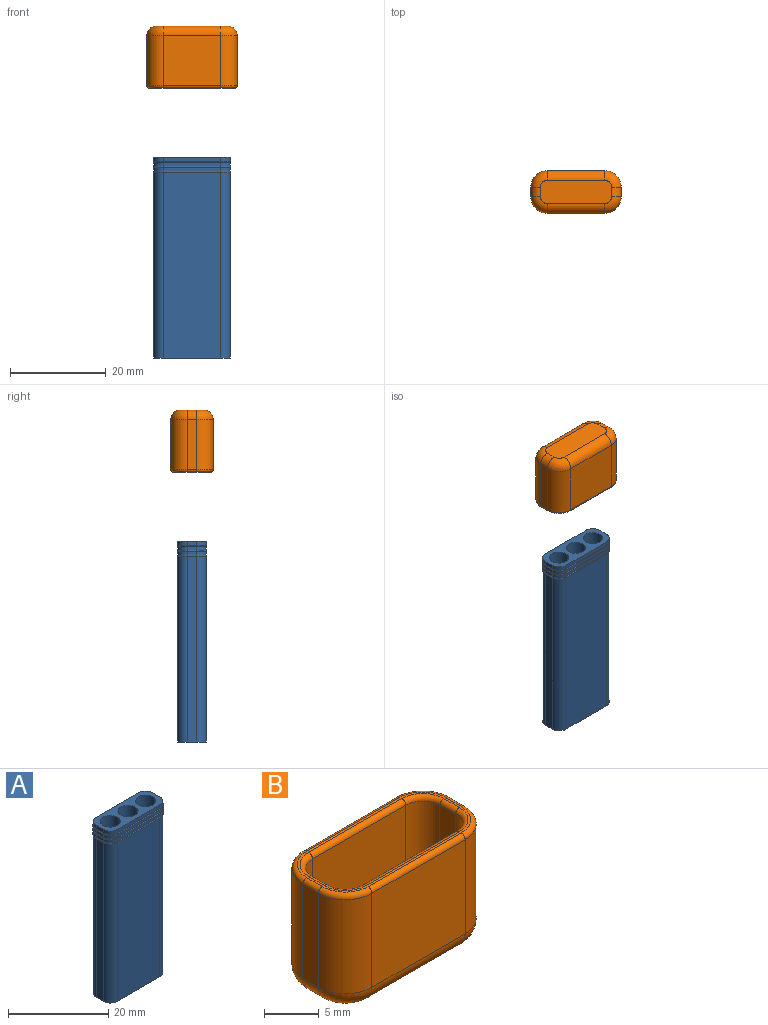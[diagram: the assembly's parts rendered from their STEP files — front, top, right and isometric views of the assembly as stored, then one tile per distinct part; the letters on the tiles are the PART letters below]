
ASSEMBLY  parts=2 mates=1
PART A: 124 faces, bbox 16.6x6.6x42 mm
  f0: plane 12x0.75mm, normal (0,-1,0), area 9mm2, adj f2,f5,f10,f47
  f1: plane 2x0.75mm, normal (-1,0,0), area 1.5mm2, adj f4,f5,f11,f48
  f2: cylinder r=2mm len=2mm, axis (0,0,-1), area 2.4mm2, adj f0,f9,f14,f51
  f3: cylinder r=2mm len=2mm, axis (0,0,1), area 2.4mm2, adj f8,f9,f12,f49
  f4: cylinder r=2mm len=2mm, axis (0,0,-1), area 2.4mm2, adj f1,f8,f16,f53
  f5: cylinder r=2mm len=2mm, axis (0,0,1), area 2.4mm2, adj f0,f1,f15,f52
  f6: plane 2x0.75mm, normal (1,0,0), area 1.5mm2, adj f13,f18,f19,f27
  f7: plane 12x0.75mm, normal (0,1,0), area 9mm2, adj f17,f19,f21,f31
  f8: plane 12x0.75mm, normal (0,1,0), area 9mm2, adj f3,f4,f17,f54
  f9: plane 2x0.75mm, normal (1,0,0), area 1.5mm2, adj f2,f3,f13,f50
  f10: cylinder r=0.12mm len=12mm, axis (1,0,0), area 4.7mm2, adj f0,f14,f15,f23
  f11: cylinder r=0.12mm len=2mm, axis (0,-1,0), area 0.8mm2, adj f1,f15,f16,f22
  f12: torus R=2mm, axis (0,0,1), area 1.3mm2, adj f3,f13,f17,f19
  f13: cylinder r=0.12mm len=2mm, axis (0,1,0), area 0.8mm2, adj f6,f9,f12,f14
  f14: torus R=2mm, axis (0,0,1), area 1.3mm2, adj f2,f10,f13,f18
  f15: torus R=2mm, axis (0,0,1), area 1.3mm2, adj f5,f10,f11,f20
  f16: torus R=2mm, axis (0,0,1), area 1.3mm2, adj f4,f11,f17,f21
  f17: cylinder r=0.12mm len=12mm, axis (-1,0,0), area 4.7mm2, adj f7,f8,f12,f16
  f18: cylinder r=2mm len=2mm, axis (0,0,-1), area 2.4mm2, adj f6,f14,f23,f28
  f19: cylinder r=2mm len=2mm, axis (0,0,1), area 2.4mm2, adj f6,f7,f12,f26
  f20: cylinder r=2mm len=2mm, axis (0,0,1), area 2.4mm2, adj f15,f22,f23,f29
  f21: cylinder r=2mm len=2mm, axis (0,0,-1), area 2.4mm2, adj f7,f16,f22,f30
  f22: plane 2x0.75mm, normal (-1,0,0), area 1.5mm2, adj f11,f20,f21,f24
  f23: plane 12x0.75mm, normal (0,-1,0), area 9mm2, adj f10,f18,f20,f25
  f24: cylinder r=0.12mm len=2mm, axis (0,-1,0), area 0.8mm2, adj f22,f29,f30,f41
  f25: cylinder r=0.12mm len=12mm, axis (1,0,0), area 4.7mm2, adj f23,f28,f29,f43
  f26: torus R=2mm, axis (0,0,1), area 1.3mm2, adj f19,f27,f31,f45
  f27: cylinder r=0.12mm len=2mm, axis (0,1,0), area 0.8mm2, adj f6,f26,f28,f39
  f28: torus R=2mm, axis (0,0,1), area 1.3mm2, adj f18,f25,f27,f46
  f29: torus R=2mm, axis (0,0,1), area 1.3mm2, adj f20,f24,f25,f44
  f30: torus R=2mm, axis (0,0,1), area 1.3mm2, adj f21,f24,f31,f42
  f31: cylinder r=0.12mm len=12mm, axis (-1,0,0), area 4.7mm2, adj f7,f26,f30,f40
  f32: plane 2x2mm, normal (0,0,1), area 3.1mm2, adj f123
  f33: plane 2x2mm, normal (0,0,1), area 3.1mm2, adj f122
  f34: plane 2x2mm, normal (0,0,1), area 3.1mm2, adj f121
  f35: cylinder r=2mm len=39mm, axis (0,0,-1), area 490.1mm2, adj f38,f123
  f36: cylinder r=2mm len=39mm, axis (0,0,-1), area 490.1mm2, adj f38,f122
  f37: cylinder r=2mm len=39mm, axis (0,0,-1), area 490.1mm2, adj f38,f121
  f38: plane 16x6mm, normal (0,0,1), area 54.9mm2, adj f35,f36,f37,f39,f40,f41,f42,f43
  f39: plane 2x0.88mm, normal (1,0,0), area 1.8mm2, adj f27,f38,f45,f46
  f40: plane 12x0.88mm, normal (0,1,0), area 10.5mm2, adj f31,f38,f42,f45
  f41: plane 2x0.88mm, normal (-1,0,0), area 1.8mm2, adj f24,f38,f42,f44
  f42: cylinder r=2mm len=2mm, axis (0,0,-1), area 2.7mm2, adj f30,f38,f40,f41
  f43: plane 12x0.88mm, normal (0,-1,0), area 10.5mm2, adj f25,f38,f44,f46
  f44: cylinder r=2mm len=2mm, axis (0,0,1), area 2.7mm2, adj f29,f38,f41,f43
  f45: cylinder r=2mm len=2mm, axis (0,0,1), area 2.7mm2, adj f26,f38,f39,f40
  f46: cylinder r=2mm len=2mm, axis (0,0,-1), area 2.7mm2, adj f28,f38,f39,f43
  f47: cylinder r=0.12mm len=12mm, axis (1,0,0), area 4.7mm2, adj f0,f51,f52,f118
  f48: cylinder r=0.12mm len=2mm, axis (0,-1,0), area 0.8mm2, adj f1,f52,f53,f116
  f49: torus R=2mm, axis (0,0,1), area 1.3mm2, adj f3,f50,f54,f113
  f50: cylinder r=0.12mm len=2mm, axis (0,1,0), area 0.8mm2, adj f9,f49,f51,f119
  f51: torus R=2mm, axis (0,0,1), area 1.3mm2, adj f2,f47,f50,f117
  f52: torus R=2mm, axis (0,0,1), area 1.3mm2, adj f5,f47,f48,f115
  f53: torus R=2mm, axis (0,0,1), area 1.3mm2, adj f4,f48,f54,f114
  f54: cylinder r=0.12mm len=12mm, axis (-1,0,0), area 4.7mm2, adj f8,f49,f53,f120
  f55: plane 4.39x3.01mm, normal (0,1,0), area 6.3mm2, adj f56,f57,f58,f59,f60,f61
  f56: extruded ~1.75x0.25mm, area 0.4mm2, adj f55,f57,f61,f65
  f57: plane 0.25x0.04mm, normal (1,0,0), area 0mm2, adj f55,f56,f58,f65
  f58: extruded ~0.86x0.49mm, area 0.2mm2, adj f55,f57,f59,f65
  f59: plane 3.53x2.48mm, normal (0.58,0,-0.82), area 1.1mm2, adj f55,f58,f60,f65
  f60: plane 2.96x0.25mm, normal (-1,0,0), area 0.7mm2, adj f55,f59,f61,f65
  f61: plane 2.64x0.25mm, normal (0,0,1), area 0.7mm2, adj f55,f56,f60,f65
  f62: plane 7.93x7.86mm, normal (0,1,0), area 26.9mm2, adj f66,f67,f68,f69,f70,f71,f72,f73
  f63: plane 7.93x2.86mm, normal (0,1,0), area 8.6mm2, adj f84,f85,f86,f87,f88,f89,f90,f91
  f64: plane 1.47x1.31mm, normal (0,1,0), area 1.6mm2, adj f93,f94,f95,f96,f97,f98,f99,f100
  f65: plane 7.98x5.9mm, normal (0,1,0), area 15.2mm2, adj f56,f57,f58,f59,f60,f61,f101,f102
  f66: plane 7.02x2.71mm, normal (0.36,0,-0.93), area 1.9mm2, adj f62,f67,f83,f120
  f67: plane 0.25x0.04mm, normal (1,0,0), area 0mm2, adj f62,f66,f68,f120
  f68: extruded ~1.91x0.25mm, area 0.5mm2, adj f62,f67,f69,f120
  f69: plane 5.11x0.25mm, normal (0,0,1), area 1.3mm2, adj f62,f68,f70,f120
  f70: plane 0.92x0.25mm, normal (1,0,0), area 0.2mm2, adj f62,f69,f71,f120
  f71: plane 7.93x0.25mm, normal (0,0,-1), area 2mm2, adj f62,f70,f72,f120
  f72: plane 1.38x0.25mm, normal (-1,0,0), area 0.3mm2, adj f62,f71,f73,f120
  f73: plane 6.54x2.53mm, normal (-0.36,0,0.93), area 1.8mm2, adj f62,f72,f74,f120
  f74: plane 0.25x0.04mm, normal (-1,0,0), area 0mm2, adj f62,f73,f75,f120
  f75: plane 6.54x2.51mm, normal (-0.36,0,-0.93), area 1.8mm2, adj f62,f74,f76,f120
  f76: plane 1.39x0.25mm, normal (-1,0,0), area 0.3mm2, adj f62,f75,f77,f120
  f77: plane 7.93x0.25mm, normal (0,0,1), area 2mm2, adj f62,f76,f78,f120
  f78: plane 0.85x0.25mm, normal (1,0,0), area 0.2mm2, adj f62,f77,f79,f120
  f79: plane 5.05x0.25mm, normal (0,0,-1), area 1.3mm2, adj f62,f78,f80,f120
  f80: extruded ~1.99x0.25mm, area 0.5mm2, adj f62,f79,f81,f120
  f81: plane 0.25x0.04mm, normal (1,0,0), area 0mm2, adj f62,f80,f82,f120
  f82: plane 7.03x2.69mm, normal (0.36,0,0.93), area 1.9mm2, adj f62,f81,f83,f120
  f83: plane 0.74x0.25mm, normal (1,0,0), area 0.2mm2, adj f62,f66,f82,f120
  f84: plane 0.76x0.25mm, normal (-1,0,0), area 0.2mm2, adj f63,f85,f92,f120
  f85: plane 2.1x1.62mm, normal (-0.79,0,0.61), area 0.7mm2, adj f63,f84,f86,f120
  f86: plane 0.62x0.48mm, normal (0.61,0,0.79), area 0.2mm2, adj f63,f85,f87,f120
  f87: extruded ~1.29x1.06mm, area 0.4mm2, adj f63,f86,f88,f120
  f88: extruded ~0.25x0.25mm, area 0.1mm2, adj f63,f87,f89,f120
  f89: extruded ~1.34x0.25mm, area 0.3mm2, adj f63,f88,f90,f120
  f90: plane 5.65x0.25mm, normal (0,0,1), area 1.4mm2, adj f63,f89,f91,f120
  f91: plane 0.88x0.25mm, normal (1,0,0), area 0.2mm2, adj f63,f90,f92,f120
  f92: plane 7.93x0.25mm, normal (0,0,-1), area 2mm2, adj f63,f84,f91,f120
  f93: extruded ~0.46x0.25mm, area 0.1mm2, adj f64,f94,f100,f120
  f94: extruded ~0.49x0.25mm, area 0.1mm2, adj f64,f93,f95,f120
  f95: extruded ~0.54x0.25mm, area 0.1mm2, adj f64,f94,f96,f120
  f96: extruded ~0.55x0.25mm, area 0.1mm2, adj f64,f95,f97,f120
  f97: extruded ~0.49x0.25mm, area 0.1mm2, adj f64,f96,f98,f120
  f98: extruded ~0.48x0.25mm, area 0.1mm2, adj f64,f97,f99,f120
  f99: extruded ~0.55x0.25mm, area 0.1mm2, adj f64,f98,f100,f120
  f100: extruded ~0.56x0.25mm, area 0.2mm2, adj f64,f93,f99,f120
  f101: plane 1.18x0.25mm, normal (-1,0,0), area 0.3mm2, adj f65,f102,f111,f120
  f102: plane 5.33x0.25mm, normal (0,0,-1), area 1.3mm2, adj f65,f101,f103,f120
  f103: plane 0.96x0.25mm, normal (-1,0,0), area 0.2mm2, adj f65,f102,f104,f120
  f104: plane 5.37x3.77mm, normal (-0.57,0,0.82), area 1.6mm2, adj f65,f103,f105,f120
  f105: plane 0.79x0.25mm, normal (0,0,1), area 0.2mm2, adj f65,f104,f106,f120
  f106: plane 3.86x0.25mm, normal (1,0,0), area 1mm2, adj f65,f105,f107,f120
  f107: plane 1.82x0.25mm, normal (0,0,1), area 0.5mm2, adj f65,f106,f108,f120
  f108: plane 0.86x0.25mm, normal (1,0,0), area 0.2mm2, adj f65,f107,f109,f120
  f109: plane 1.82x0.25mm, normal (0,0,-1), area 0.5mm2, adj f65,f108,f110,f120
  f110: plane 1.18x0.25mm, normal (1,0,0), area 0.3mm2, adj f65,f109,f111,f120
  f111: plane 0.82x0.25mm, normal (0,0,-1), area 0.2mm2, adj f65,f101,f110,f120
  f112: plane 16x6mm, normal (0,0,-1), area 92.6mm2, adj f113,f114,f115,f116,f117,f118,f119,f120
  f113: cylinder r=2mm len=38.88mm, axis (0,0,1), area 122.1mm2, adj f49,f112,f119,f120
  f114: cylinder r=2mm len=38.88mm, axis (0,0,-1), area 122.1mm2, adj f53,f112,f116,f120
  f115: cylinder r=2mm len=38.88mm, axis (0,0,1), area 122.1mm2, adj f52,f112,f116,f118
  f116: plane 38.88x2mm, normal (-1,0,0), area 77.7mm2, adj f48,f112,f114,f115
  f117: cylinder r=2mm len=38.88mm, axis (0,0,-1), area 122.1mm2, adj f51,f112,f118,f119
  f118: plane 38.88x12mm, normal (0,-1,0), area 466.5mm2, adj f47,f112,f115,f117
  f119: plane 38.88x2mm, normal (1,0,0), area 77.7mm2, adj f50,f112,f113,f117
  f120: plane 38.88x12mm, normal (0,1,0), area 407.9mm2, adj f54,f66,f67,f68,f69,f70,f71,f72
  f121: torus R=1mm, axis (0,0,1), area 16.2mm2, adj f34,f37
  f122: torus R=1mm, axis (0,0,1), area 16.2mm2, adj f33,f36
  f123: torus R=1mm, axis (0,0,1), area 16.2mm2, adj f32,f35
PART B: 43 faces, bbox 19.5x9.5x13 mm
  f0: plane 12x9.5mm, normal (0,-1,0), area 114mm2, adj f1,f15,f17,f23
  f1: cylinder r=2.2mm len=9.5mm, axis (0,0,-1), area 32.8mm2, adj f0,f2,f17,f21
  f2: plane 9.5x2mm, normal (-1,0,0), area 19mm2, adj f1,f3,f17,f19
  f3: cylinder r=2.2mm len=9.5mm, axis (0,0,-1), area 32.8mm2, adj f2,f4,f17,f20
  f4: plane 12x9.5mm, normal (0,1,0), area 114mm2, adj f3,f5,f17,f22
  f5: cylinder r=2.2mm len=9.5mm, axis (0,0,-1), area 32.8mm2, adj f4,f6,f17,f24
  f6: plane 9.5x2mm, normal (1,0,0), area 19mm2, adj f5,f15,f17,f26
  f7: cylinder r=3.45mm len=10.5mm, axis (0,0,-1), area 56.9mm2, adj f8,f14,f32,f38
  f8: plane 12x10.5mm, normal (0,1,0), area 126mm2, adj f7,f9,f30,f36
  f9: cylinder r=3.45mm len=10.5mm, axis (0,0,-1), area 56.9mm2, adj f8,f10,f28,f35
  f10: plane 10.5x2mm, normal (-1,0,0), area 21mm2, adj f9,f11,f27,f37
  f11: cylinder r=3.45mm len=10.5mm, axis (0,0,-1), area 56.9mm2, adj f10,f12,f29,f39
  f12: plane 12x10.5mm, normal (0,-1,0), area 126mm2, adj f11,f13,f31,f41
  f13: cylinder r=3.45mm len=10.5mm, axis (0,0,-1), area 56.9mm2, adj f12,f14,f33,f42
  f14: plane 10.5x2mm, normal (1,0,0), area 21mm2, adj f7,f13,f34,f40
  f15: cylinder r=2.2mm len=9.5mm, axis (0,0,-1), area 32.8mm2, adj f0,f6,f17,f25
  f16: plane 17.9x7.9mm, normal (0,0,1), area 11.4mm2, adj f19,f20,f21,f22,f23,f24,f25,f26
  f17: plane 16.4x6.4mm, normal (0,0,1), area 100.8mm2, adj f0,f1,f2,f3,f4,f5,f6,f15
  f18: plane 14.9x4.9mm, normal (0,0,-1), area 71.2mm2, adj f35,f36,f37,f38,f39,f40,f41,f42
  f19: cylinder r=0.5mm len=2mm, axis (0,1,0), area 1.6mm2, adj f2,f16,f20,f21
  f20: torus R=2.7mm, axis (0,0,1), area 2.9mm2, adj f3,f16,f19,f22
  f21: torus R=2.7mm, axis (0,0,1), area 2.9mm2, adj f1,f16,f19,f23
  f22: cylinder r=0.5mm len=12mm, axis (1,0,0), area 9.4mm2, adj f4,f16,f20,f24
  f23: cylinder r=0.5mm len=12mm, axis (-1,0,0), area 9.4mm2, adj f0,f16,f21,f25
  f24: torus R=2.7mm, axis (0,0,1), area 2.9mm2, adj f5,f16,f22,f26
  f25: torus R=2.7mm, axis (0,0,1), area 2.9mm2, adj f15,f16,f23,f26
  f26: cylinder r=0.5mm len=2mm, axis (0,-1,0), area 1.6mm2, adj f6,f16,f24,f25
  f27: cylinder r=0.5mm len=2mm, axis (0,1,0), area 1.6mm2, adj f10,f16,f28,f29
  f28: torus R=2.95mm, axis (0,0,1), area 4mm2, adj f9,f16,f27,f30
  f29: torus R=2.95mm, axis (0,0,1), area 4mm2, adj f11,f16,f27,f31
  f30: cylinder r=0.5mm len=12mm, axis (1,0,0), area 9.4mm2, adj f8,f16,f28,f32
  f31: cylinder r=0.5mm len=12mm, axis (-1,0,0), area 9.4mm2, adj f12,f16,f29,f33
  f32: torus R=2.95mm, axis (0,0,1), area 4mm2, adj f7,f16,f30,f34
  f33: torus R=2.95mm, axis (0,0,1), area 4mm2, adj f13,f16,f31,f34
  f34: cylinder r=0.5mm len=2mm, axis (0,-1,0), area 1.6mm2, adj f14,f16,f32,f33
  f35: torus R=1.45mm, axis (0,0,1), area 13.4mm2, adj f9,f18,f36,f37
  f36: cylinder r=2mm len=12mm, axis (-1,0,0), area 37.7mm2, adj f8,f18,f35,f38
  f37: cylinder r=2mm len=2mm, axis (0,-1,0), area 6.3mm2, adj f10,f18,f35,f39
  f38: torus R=1.45mm, axis (0,0,1), area 13.4mm2, adj f7,f18,f36,f40
  f39: torus R=1.45mm, axis (0,0,1), area 13.4mm2, adj f11,f18,f37,f41
  f40: cylinder r=2mm len=2mm, axis (0,1,0), area 6.3mm2, adj f14,f18,f38,f42
  f41: cylinder r=2mm len=12mm, axis (1,0,0), area 37.7mm2, adj f12,f18,f39,f42
  f42: torus R=1.45mm, axis (0,0,1), area 13.4mm2, adj f13,f18,f40,f41
PLACE A t=(0,0,-22.1)mm
PLACE B rot(axis=(1,0,0),180deg) t=(0,0,42.4)mm
MATE slider B.f17 <-> A.f35  axis (0,0,-1) through (0,0,42.4)mm
